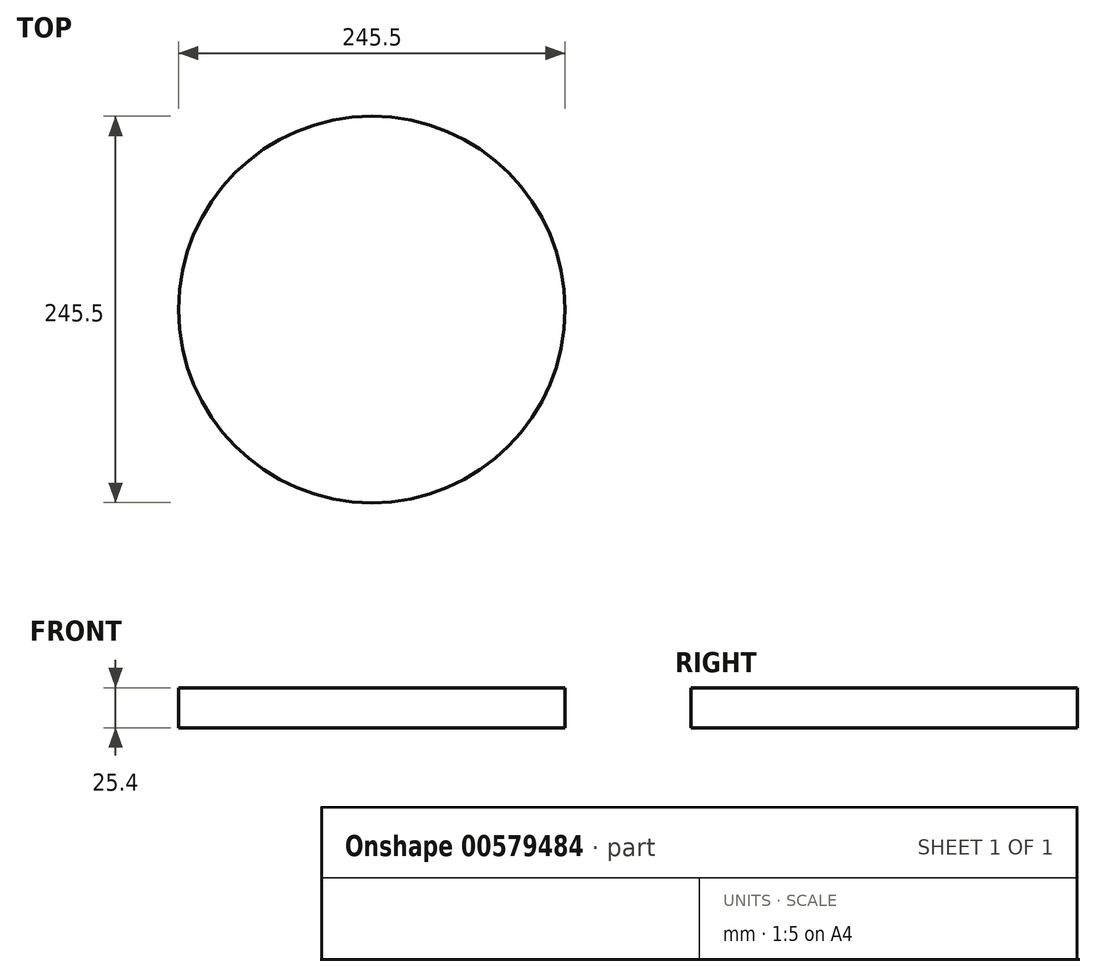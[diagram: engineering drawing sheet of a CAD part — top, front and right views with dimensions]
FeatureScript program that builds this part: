
annotation { "Feature Type Name" : "Feature", "Feature Type Description" : "" }
export const myFeature = defineFeature(function(context is Context, id is Id, definition is map)
    precondition{}
    {
        {
            var Q0;
            Q0=qCreatedBy(makeId("Top.planeOp"),FACE);
            var sketch = newSketch(context, id + "F0", { "sketchPlane" : qUnion([Q0])});
            skCircle(sketch, "E0", {"center": v(-84.99, 43.06) * mm, "radius": 122.75 * mm});
            skSolve(sketch);
        }
        {
            var Q0;
            Q0=makeQuery(id+"F0.imprint","IMPRINT",FACE,{"disambiguationData":[TD([[makeQuery(id+"F0.imprint","IMPRINT",EDGE,{"derivedFrom":sQuery(id+"F0.wireOp",EDGE,"E0")}),1.0]])]});
            extrude(context, id + "F1", {"entities" : qUnion([Q0]), "depth" : 25.4 * mm, "offsetDistance" : 25.4 * mm});
        }
    });
